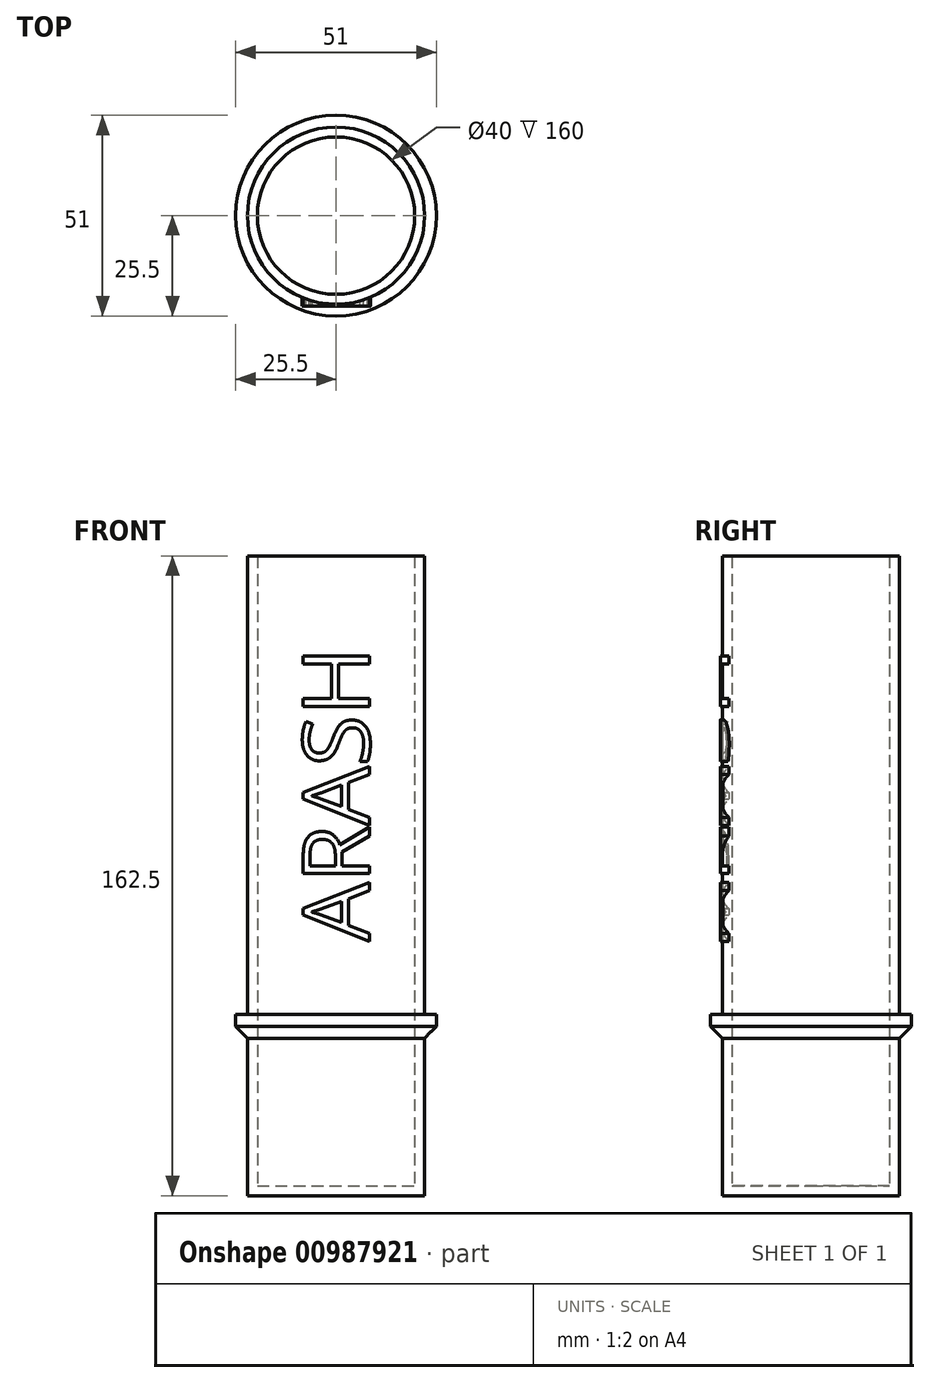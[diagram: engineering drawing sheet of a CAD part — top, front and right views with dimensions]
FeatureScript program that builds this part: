
annotation { "Feature Type Name" : "Feature", "Feature Type Description" : "" }
export const myFeature = defineFeature(function(context is Context, id is Id, definition is map)
    precondition{}
    {
        {
            var Q0;
            Q0=qCreatedBy(makeId("Front.planeOp"),FACE);
            var sketch = newSketch(context, id + "F0", { "sketchPlane" : qUnion([Q0])});
            skLineSegment(sketch, "E0", {"start": v(0, 0) * mm, "end": v(20, 0) * mm});
            skLineSegment(sketch, "E1", {"start": v(20, 0) * mm, "end": v(20, 160) * mm});
            skLineSegment(sketch, "E2", {"start": v(20, 160) * mm, "end": v(22.5, 160) * mm});
            skLineSegment(sketch, "E3", {"start": v(22.5, 160) * mm, "end": v(22.5, -2.5) * mm});
            skLineSegment(sketch, "E4", {"start": v(22.5, -2.5) * mm, "end": v(0, -2.5) * mm});
            skLineSegment(sketch, "E5", {"start": v(0, -2.5) * mm, "end": v(0, 0) * mm});
            skSolve(sketch);
        }
        {
            var Q0;
            Q0=makeQuery(id+"F0.imprint","IMPRINT",FACE,{"disambiguationData":[TD([[makeQuery(id+"F0.imprint","IMPRINT",EDGE,{"derivedFrom":sQuery(id+"F0.wireOp",EDGE,"E0")}),-1.0]])]});
            var Q1;
            Q1=sQuery(id+"F0.wireOp",EDGE,"E5");
            revolve(context, id + "F1", {"surfaceOperationType" : NewSurfaceOperationType.NEW, "entities" : qUnion([Q0]), "axis" : qUnion([Q1]), "revolveType" : RevolveType.FULL});
        }
        {
            var Q0;
            Q0=qCreatedBy(makeId("Front.planeOp"),FACE);
            var sketch = newSketch(context, id + "F2", { "sketchPlane" : qUnion([Q0])});
            skLineSegment(sketch, "E6", {"start": v(22.5, 43.5) * mm, "end": v(22.5, 37.5) * mm});
            skLineSegment(sketch, "E7", {"start": v(22.5, 43.5) * mm, "end": v(25.5, 43.5) * mm});
            skLineSegment(sketch, "E8", {"start": v(25.5, 43.5) * mm, "end": v(25.5, 40.5) * mm});
            skLineSegment(sketch, "E9", {"start": v(25.5, 40.5) * mm, "end": v(22.5, 37.5) * mm});
            skLineSegment(sketch, "E10", {"start": v(0, 0) * mm, "end": v(0, 39.21) * mm});
            skSolve(sketch);
        }
        {
            var Q0;
            Q0=makeQuery(id+"F2.imprint","IMPRINT",FACE,{"disambiguationData":[TD([[makeQuery(id+"F2.imprint","IMPRINT",EDGE,{"derivedFrom":sQuery(id+"F2.wireOp",EDGE,"E6")}),1.0]])]});
            var Q1;
            Q1=sQuery(id+"F2.wireOp",EDGE,"E10");
            revolve(context, id + "F3", {"operationType" : NewBodyOperationType.ADD, "surfaceOperationType" : NewSurfaceOperationType.NEW, "entities" : qUnion([Q0]), "axis" : qUnion([Q1]), "revolveType" : RevolveType.FULL});
        }
        {
            var Q0;
            Q0=qCreatedBy(makeId("Front.planeOp"),FACE);
            cPlane(context, id + "F4", {"entities" : qUnion([Q0]), "cplaneType" : CPlaneType.OFFSET, "offset" : 20 * mm, "width" : 150 * mm, "height" : 150 * mm});
        }
        {
            var Q0;
            Q0=qCreatedBy(id+"F4.planeOp",FACE);
            var sketch = newSketch(context, id + "F5", { "sketchPlane" : qUnion([Q0])});
            skText(sketch, "E11", { "text": "ARASH", "fontName": "OpenSans-Regular.ttf"});
            skPoint(sketch, "E12", {"position": v(0, 62.12) * mm});
            const initialGuessF5  = {"E11": [0.0085, 0.06212, 0, 1, 0.01698]};
            skSetInitialGuess(sketch, initialGuessF5);
            skSolve(sketch);
        }
        {
            var Q0;
            Q0 = qSketchRegion(id + "F5", true);
            extrude(context, id + "F6", {"entities" : qUnion([Q0]), "operationType" : NewBodyOperationType.ADD, "depth" : 3 * mm, "offsetDistance" : 25 * mm});
        }
    });
